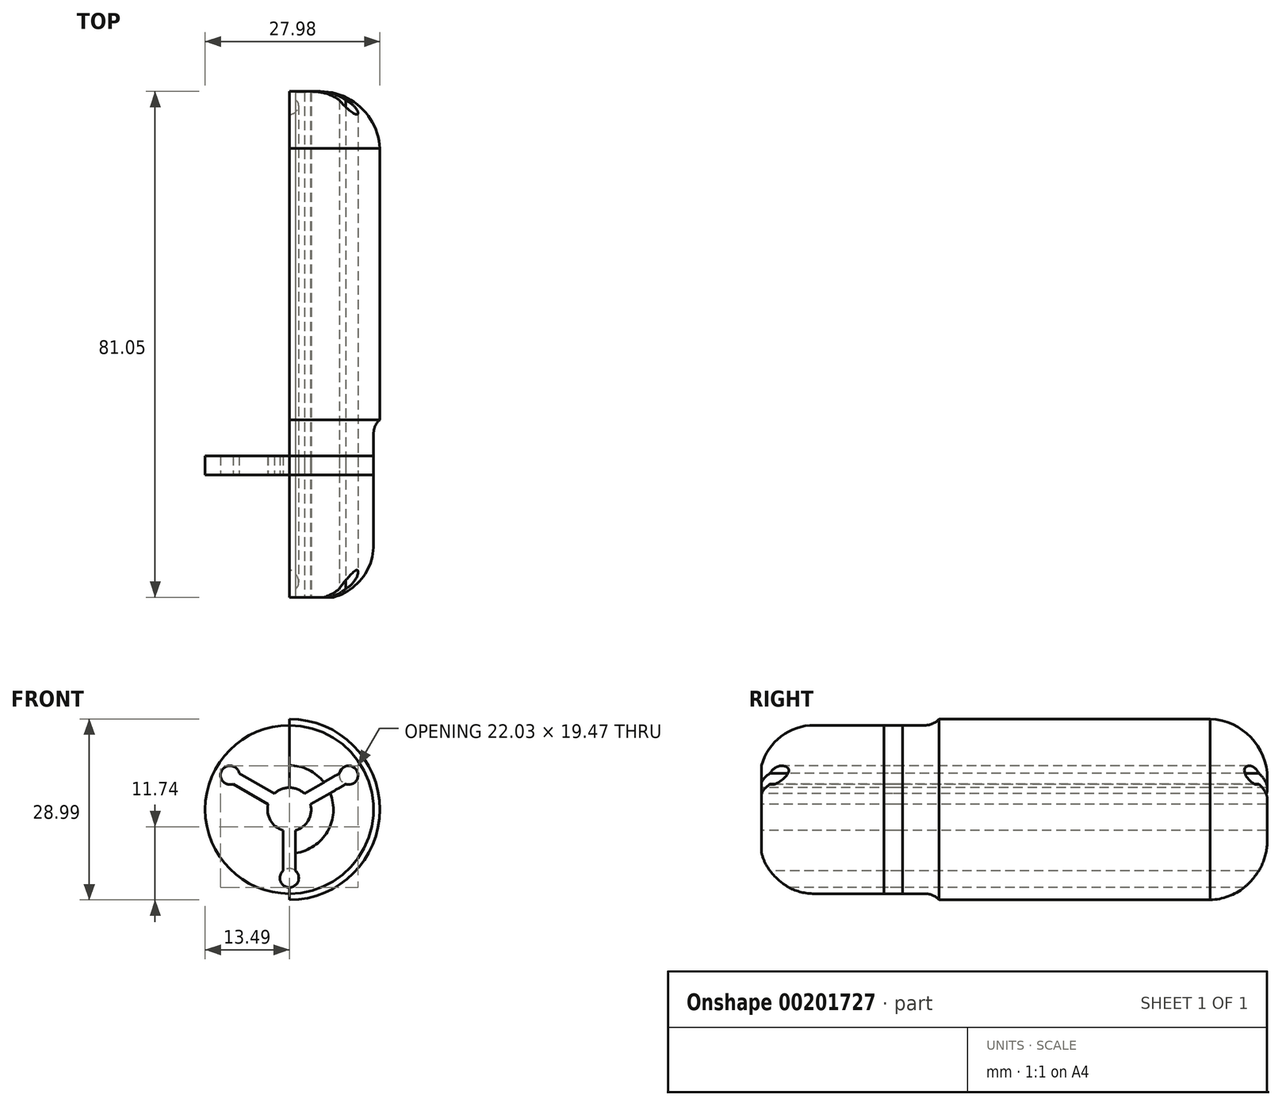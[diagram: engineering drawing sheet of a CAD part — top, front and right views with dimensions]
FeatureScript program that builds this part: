
annotation { "Feature Type Name" : "Feature", "Feature Type Description" : "" }
export const myFeature = defineFeature(function(context is Context, id is Id, definition is map)
    precondition{}
    {
        {
            var Q0;
            Q0=qCreatedBy(makeId("Right.planeOp"),FACE);
            var sketch = newSketch(context, id + "F0", { "sketchPlane" : qUnion([Q0])});
            skLineSegment(sketch, "E0.bottom", {"start": v(-3.13, 33.38) * mm, "end": v(86.87, 33.38) * mm});
            skLineSegment(sketch, "E0.top", {"start": v(-3.13, 32.38) * mm, "end": v(4.08, 32.38) * mm});
            skLineSegment(sketch, "E0.left", {"start": v(-3.13, 33.38) * mm, "end": v(-3.13, 32.38) * mm});
            skLineSegment(sketch, "E0.right", {"start": v(86.87, 33.38) * mm, "end": v(86.87, 32.38) * mm});
            skPoint(sketch, "E0.middle", {"position": v(41.87, 32.88) * mm});
            skLineSegment(sketch, "E1.bottom", {"start": v(86.87, 32.38) * mm, "end": v(81.87, 32.38) * mm, "construction": true});
            skLineSegment(sketch, "E1.top", {"start": v(86.87, 21.38) * mm, "end": v(85.87, 21.38) * mm});
            skLineSegment(sketch, "E1.left", {"start": v(86.87, 32.38) * mm, "end": v(86.87, 21.38) * mm, "construction": true});
            skLineSegment(sketch, "E1.right", {"start": v(81.87, 32.38) * mm, "end": v(81.87, 21.38) * mm, "construction": true});
            skLineSegment(sketch, "E2.bottom", {"start": v(81.87, 32.38) * mm, "end": v(71.87, 32.38) * mm, "construction": true});
            skLineSegment(sketch, "E2.top", {"start": v(81.87, 21.38) * mm, "end": v(71.87, 21.38) * mm, "construction": true});
            skLineSegment(sketch, "E2.right", {"start": v(71.87, 33.38) * mm, "end": v(71.87, 21.38) * mm, "construction": true});
            skLineSegment(sketch, "E3.0", {"start": v(85.87, 22.38) * mm, "end": v(85.37, 22.38) * mm, "construction": true});
            skLineSegment(sketch, "E4.0", {"start": v(85.87, 32.38) * mm, "end": v(85.87, 21.38) * mm, "construction": true});
            skArc(sketch, "E5", {"start": v(82.3, 22.38) * mm, "mid": v(80.84, 28.3) * mm, "end": v(76.33, 32.38) * mm});
            skArc(sketch, "E6", {"start": v(81.87, 21.38) * mm, "mid": v(79.3, 29.1) * mm, "end": v(71.87, 32.38) * mm});
            skLineSegment(sketch, "E7.trimOffspring", {"start": v(76.33, 32.38) * mm, "end": v(86.87, 32.38) * mm});
            skLineSegment(sketch, "E8.top", {"start": v(86.87, 25.38) * mm, "end": v(85.87, 25.38) * mm});
            skLineSegment(sketch, "E8.left", {"start": v(86.87, 23.38) * mm, "end": v(86.87, 25.38) * mm});
            skLineSegment(sketch, "E8.right", {"start": v(85.87, 22.38) * mm, "end": v(85.87, 22.72) * mm, "construction": true});
            skLineSegment(sketch, "E9.bottom", {"start": v(-3.13, 32.38) * mm, "end": v(-2.13, 32.38) * mm, "construction": true});
            skLineSegment(sketch, "E9.top", {"start": v(-3.13, 21.38) * mm, "end": v(-2.13, 21.38) * mm});
            skLineSegment(sketch, "E9.left", {"start": v(-3.13, 32.38) * mm, "end": v(-3.13, 21.38) * mm, "construction": true});
            skLineSegment(sketch, "E9.right", {"start": v(-2.13, 32.38) * mm, "end": v(-2.13, 21.38) * mm, "construction": true});
            skLineSegment(sketch, "E10.bottom", {"start": v(-2.13, 32.38) * mm, "end": v(4.08, 32.38) * mm, "construction": true});
            skLineSegment(sketch, "E10.top", {"start": v(-2.13, 33.38) * mm, "end": v(8.87, 33.38) * mm, "construction": true});
            skLineSegment(sketch, "E10.left", {"start": v(-2.13, 32.38) * mm, "end": v(-2.13, 33.38) * mm, "construction": true});
            skLineSegment(sketch, "E10.right", {"start": v(8.87, 32.38) * mm, "end": v(8.87, 33.38) * mm, "construction": true});
            skArc(sketch, "E11", {"start": v(4.08, 32.38) * mm, "mid": v(-1.17, 27.96) * mm, "end": v(-3.13, 21.38) * mm});
            skArc(sketch, "E12", {"start": v(8.87, 32.38) * mm, "mid": v(1.1, 29.16) * mm, "end": v(-2.13, 21.38) * mm});
            skLineSegment(sketch, "E13.trimOffspring", {"start": v(8.87, 32.38) * mm, "end": v(71.87, 32.38) * mm});
            skLineSegment(sketch, "E14", {"start": v(8.87, 21.38) * mm, "end": v(71.87, 21.38) * mm, "construction": true});
            skLineSegment(sketch, "E15.0", {"start": v(8.87, 17.38) * mm, "end": v(71.87, 17.38) * mm, "construction": true});
            skLineSegment(sketch, "E16.0", {"start": v(86.87, 23.38) * mm, "end": v(85.87, 23.38) * mm, "construction": true});
            skLineSegment(sketch, "E17.0", {"start": v(83.87, 21.38) * mm, "end": v(83.87, 25.38) * mm, "construction": true});
            skLineSegment(sketch, "E18", {"start": v(86.87, 23.38) * mm, "end": v(83.87, 21.38) * mm});
            skLineSegment(sketch, "E19.0", {"start": v(85.87, 23.92) * mm, "end": v(83.57, 22.38) * mm});
            skLineSegment(sketch, "E20.trimOffspring", {"start": v(83.87, 21.38) * mm, "end": v(81.87, 21.38) * mm});
            skLineSegment(sketch, "E21.trimOffspring", {"start": v(83.57, 22.38) * mm, "end": v(82.3, 22.38) * mm});
            skLineSegment(sketch, "E22.trimOffspring", {"start": v(85.87, 23.92) * mm, "end": v(85.87, 25.38) * mm});
            skLineSegment(sketch, "E23.bottom", {"start": v(8.87, 17.38) * mm, "end": v(-3.13, 17.38) * mm, "construction": true});
            skLineSegment(sketch, "E23.top", {"start": v(8.87, 21.38) * mm, "end": v(-3.13, 21.38) * mm, "construction": true});
            skLineSegment(sketch, "E23.left", {"start": v(8.87, 17.38) * mm, "end": v(8.87, 21.38) * mm, "construction": true});
            skLineSegment(sketch, "E23.right", {"start": v(-3.13, 17.38) * mm, "end": v(-3.13, 21.38) * mm, "construction": true});
            skSolve(sketch);
        }
        {
            var Q0;
            Q0=qCreatedBy(makeId("Right.planeOp"),FACE);
            var sketch = newSketch(context, id + "F1", { "sketchPlane" : qUnion([Q0])});
            skLineSegment(sketch, "E24.bottom", {"start": v(-3.13, 33.38) * mm, "end": v(28.58, 33.38) * mm, "construction": true});
            skLineSegment(sketch, "E24.left", {"start": v(-3.13, 33.38) * mm, "end": v(-3.13, 23.38) * mm, "construction": true});
            skLineSegment(sketch, "E24.right", {"start": v(28.58, 33.38) * mm, "end": v(28.58, 33.38) * mm});
            skLineSegment(sketch, "E25", {"start": v(28.58, 32.38) * mm, "end": v(8.84, 32.38) * mm, "construction": true});
            skArc(sketch, "E26", {"start": v(8.84, 32.38) * mm, "mid": v(1.84, 29.83) * mm, "end": v(-1.88, 23.38) * mm, "construction": true});
            skLineSegment(sketch, "E27.0", {"start": v(27.9, 31.88) * mm, "end": v(8.84, 31.88) * mm});
            skArc(sketch, "E28.0", {"start": v(8.84, 31.88) * mm, "mid": v(2.16, 29.45) * mm, "end": v(-1.38, 23.3) * mm});
            skLineSegment(sketch, "E29.0", {"start": v(26.58, 31.38) * mm, "end": v(8.84, 31.38) * mm});
            skArc(sketch, "E30.0", {"start": v(8.84, 30.88) * mm, "mid": v(2.9, 28.77) * mm, "end": v(-0.35, 23.38) * mm, "construction": true});
            skPoint(sketch, "E31.newPointB", {"position": v(28.58, 23.38) * mm});
            skArc(sketch, "E31.filletArc", {"start": v(26.58, 31.38) * mm, "mid": v(27.3, 31.5) * mm, "end": v(27.9, 31.88) * mm});
            skArc(sketch, "E32", {"start": v(8.84, 31.38) * mm, "mid": v(2.64, 29.01) * mm, "end": v(-0.4, 23.12) * mm});
            skLineSegment(sketch, "E33.trimOffspring", {"start": v(-1.37, 23.38) * mm, "end": v(-0.35, 23.38) * mm});
            skSolve(sketch);
        }
        {
            var Q0;
            Q0=qCreatedBy(makeId("Right.planeOp"),FACE);
            var sketch = newSketch(context, id + "F2", { "sketchPlane" : qUnion([Q0])});
            skLineSegment(sketch, "E34", {"start": v(86.87, 23.38) * mm, "end": v(83.87, 21.38) * mm, "construction": true});
            skLineSegment(sketch, "E35", {"start": v(83.87, 21.38) * mm, "end": v(81.87, 21.38) * mm, "construction": true});
            skLineSegment(sketch, "E36.0", {"start": v(86.87, 22.78) * mm, "end": v(84.02, 20.88) * mm});
            skLineSegment(sketch, "E37.0", {"start": v(84.02, 20.88) * mm, "end": v(81.87, 20.88) * mm});
            skLineSegment(sketch, "E38", {"start": v(86.87, 22.78) * mm, "end": v(86.87, 17.38) * mm});
            skLineSegment(sketch, "E39.0", {"start": v(66.87, 20.38) * mm, "end": v(66.87, 17.38) * mm});
            skLineSegment(sketch, "E40.0", {"start": v(81.87, 20.38) * mm, "end": v(66.87, 20.38) * mm});
            skLineSegment(sketch, "E41", {"start": v(71.87, 17.38) * mm, "end": v(66.87, 17.38) * mm});
            skLineSegment(sketch, "E42", {"start": v(71.87, 17.38) * mm, "end": v(86.87, 17.38) * mm});
            skLineSegment(sketch, "E43.0", {"start": v(81.87, 20.88) * mm, "end": v(81.87, 20.38) * mm});
            skSolve(sketch);
        }
        {
            var Q0;
            Q0=qCreatedBy(makeId("Right.planeOp"),FACE);
            var sketch = newSketch(context, id + "F3", { "sketchPlane" : qUnion([Q0])});
            skArc(sketch, "E44", {"start": v(81.87, 21.38) * mm, "mid": v(79.3, 29.1) * mm, "end": v(71.87, 32.38) * mm, "construction": true});
            skArc(sketch, "E45.0", {"start": v(81.3, 20.88) * mm, "mid": v(79.25, 28.4) * mm, "end": v(72.28, 31.88) * mm});
            skLineSegment(sketch, "E46", {"start": v(81.87, 20.38) * mm, "end": v(69.18, 20.38) * mm, "construction": true});
            skLineSegment(sketch, "E47", {"start": v(28.58, 32.38) * mm, "end": v(37.05, 32.38) * mm});
            skLineSegment(sketch, "E48", {"start": v(26.58, 31.38) * mm, "end": v(22.5, 31.38) * mm});
            skArc(sketch, "E49", {"start": v(26.58, 31.38) * mm, "mid": v(27.7, 31.64) * mm, "end": v(28.58, 32.38) * mm});
            skLineSegment(sketch, "E50.0", {"start": v(28.58, 31.88) * mm, "end": v(72.28, 31.88) * mm});
            skArc(sketch, "E51.0", {"start": v(26.58, 30.88) * mm, "mid": v(27.93, 31.2) * mm, "end": v(28.98, 32.08) * mm});
            skLineSegment(sketch, "E52.0", {"start": v(26.58, 30.88) * mm, "end": v(8.74, 30.88) * mm});
            skLineSegment(sketch, "E53.0", {"start": v(81.3, 20.88) * mm, "end": v(0.37, 20.88) * mm});
            skArc(sketch, "E54", {"start": v(8.84, 31.38) * mm, "mid": v(2.74, 29.11) * mm, "end": v(-0.35, 23.38) * mm, "construction": true});
            skArc(sketch, "E55.0", {"start": v(8.83, 30.88) * mm, "mid": v(3.5, 29.1) * mm, "end": v(0.37, 24.44) * mm});
            skLineSegment(sketch, "E56", {"start": v(-2.13, 27.58) * mm, "end": v(-2.13, 15.19) * mm, "construction": true});
            skLineSegment(sketch, "E57.trimOffspring", {"start": v(0.37, 24.44) * mm, "end": v(0.37, 20.88) * mm});
            skSolve(sketch);
        }
        {
            var Q0;
            Q0=qSketchRegion(id+"F3",true);
            var Q1;
            Q1=sQuery(id+"F0.wireOp",EDGE,"E15.0");
            revolve(context, id + "F4", {"entities" : qUnion([Q0]), "axis" : qUnion([Q1]), "revolveType" : RevolveType.ONE_DIRECTION, "angle" : 180 * degree});
        }
        {
            var Q0;
            Q0=qCreatedBy(makeId("Front.planeOp"),FACE);
            var sketch = newSketch(context, id + "F5", { "sketchPlane" : qUnion([Q0])});
            skCircle(sketch, "E58", {"center": v(0, 17.38) * mm, "radius": 14.5 * mm, "construction": true});
            skCircle(sketch, "E59", {"center": v(0, 17.38) * mm, "radius": 3.5 * mm});
            skLineSegment(sketch, "E60", {"start": v(0, 17.38) * mm, "end": v(0, 4.9) * mm, "construction": true});
            skPoint(sketch, "E61", {"position": v(0, 4.9) * mm});
            skPoint(sketch, "E62", {"position": v(-16.26, 26.77) * mm});
            skLineSegment(sketch, "E63.0", {"start": v(-1, 14.03) * mm, "end": v(-1, 7.54) * mm});
            skLineSegment(sketch, "E64.0", {"start": v(1, 14.03) * mm, "end": v(1, 7.54) * mm});
            skArc(sketch, "E65", {"start": v(-1, 7.54) * mm, "mid": v(0, 4.9) * mm, "end": v(1, 7.54) * mm});
            skSolve(sketch);
        }
        {
            var Q0;
            {var subQ0=sQuery(id+"F5.wireOp",EDGE,"E63.0");Q0=makeQuery(id+"F5.imprint","IMPRINT",FACE,{"disambiguationData":[TD([[makeQuery(id+"F5.imprint","IMPRINT",EDGE,{"derivedFrom":subQ0}),1.0]])]});}
            extrude(context, id + "F6", {"entities" : qUnion([Q0]), "oppositeDirection" : true, "depth" : 90 * mm});
        }
        {
            var Q0;
            Q0=qCreatedBy(makeId("Right.planeOp"),FACE);
            var sketch = newSketch(context, id + "F7", { "sketchPlane" : qUnion([Q0])});
            skLineSegment(sketch, "E66", {"start": v(0, 17.38) * mm, "end": v(41.07, 17.38) * mm});
            skSolve(sketch);
        }
        {
            var Q0;
            Q0=makeQuery(id+"F6.opExtrude","SWEPT_BODY",BODY,{"disambiguationData":[OSD([sQuery(id+"F5.wireOp",EDGE,"E59"),sQuery(id+"F5.wireOp",EDGE,"E63.0"),sQuery(id+"F5.wireOp",EDGE,"E64.0"),sQuery(id+"F5.wireOp",EDGE,"E65")])]});
            var Q1;
            Q1=sQuery(id+"F7.wireOp",EDGE,"E66");
            circularPattern(context, id + "F8", {"entities" : qUnion([Q0]), "axis" : qUnion([Q1]), "angle" : 360 * degree, "instanceCount" : 3, "equalSpace" : true});
        }
        {
            var Q0;
            Q0=makeQuery(id+"F6.opExtrude","SWEPT_BODY",BODY,{"disambiguationData":[OSD([sQuery(id+"F5.wireOp",EDGE,"E59"),sQuery(id+"F5.wireOp",EDGE,"E63.0"),sQuery(id+"F5.wireOp",EDGE,"E64.0"),sQuery(id+"F5.wireOp",EDGE,"E65")])]});
            var Q1;
            Q1=makeQuery(id+"F8.opPattern","COPY",BODY,{"derivedFrom":makeQuery(id+"F6.opExtrude","SWEPT_BODY",BODY,{"disambiguationData":[OSD([sQuery(id+"F5.wireOp",EDGE,"E59"),sQuery(id+"F5.wireOp",EDGE,"E63.0"),sQuery(id+"F5.wireOp",EDGE,"E64.0"),sQuery(id+"F5.wireOp",EDGE,"E65")])]}),"instanceName":"2"});
            var Q2;
            Q2=makeQuery(id+"F4.opRevolve","SWEPT_BODY",BODY,{"disambiguationData":[OSD([sQuery(id+"F3.wireOp",EDGE,"E45.0"),sQuery(id+"F3.wireOp",EDGE,"E50.0"),sQuery(id+"F3.wireOp",EDGE,"E51.0"),sQuery(id+"F3.wireOp",EDGE,"E52.0"),sQuery(id+"F3.wireOp",EDGE,"E53.0"),sQuery(id+"F3.wireOp",EDGE,"E55.0"),sQuery(id+"F3.wireOp",EDGE,"E57.trimOffspring")])]});
            booleanBodies(context, id + "F9", {"operationType" : BooleanOperationType.SUBTRACTION, "tools" : qUnion([Q0, Q1]), "targets" : qUnion([Q2]), "keepTools" : true});
        }
        {
            var Q0;
            Q0 = qSketchRegion(id + "F3", true);
            var Q1;
            Q1=sQuery(id+"F0.wireOp",EDGE,"E15.0");
            revolve(context, id + "F10", {"entities" : qUnion([Q0]), "axis" : qUnion([Q1]), "revolveType" : RevolveType.FULL});
        }
        {
            var Q0;
            Q0=qCreatedBy(makeId("Front.planeOp"),FACE);
            var sketch = newSketch(context, id + "F11", { "sketchPlane" : qUnion([Q0])});
            skCircle(sketch, "E67.0", {"center": v(0, 17.38) * mm, "radius": 13.5 * mm});
            skSolve(sketch);
        }
        {
            var Q0;
            Q0 = qSketchRegion(id + "F11", true);
            extrude(context, id + "F12", {"entities" : qUnion([Q0]), "oppositeDirection" : true, "depth" : 23 * mm, "hasSecondDirection" : true, "secondDirectionOppositeDirection" : true, "secondDirectionDepth" : 20 * mm});
        }
        {
            var Q0;
            Q0=makeQuery(id+"F6.opExtrude","SWEPT_BODY",BODY,{"disambiguationData":[OSD([sQuery(id+"F5.wireOp",EDGE,"E59"),sQuery(id+"F5.wireOp",EDGE,"E63.0"),sQuery(id+"F5.wireOp",EDGE,"E64.0"),sQuery(id+"F5.wireOp",EDGE,"E65")])]});
            var Q1;
            Q1=makeQuery(id+"F8.opPattern","COPY",BODY,{"derivedFrom":makeQuery(id+"F6.opExtrude","SWEPT_BODY",BODY,{"disambiguationData":[OSD([sQuery(id+"F5.wireOp",EDGE,"E59"),sQuery(id+"F5.wireOp",EDGE,"E63.0"),sQuery(id+"F5.wireOp",EDGE,"E64.0"),sQuery(id+"F5.wireOp",EDGE,"E65")])]}),"instanceName":"2"});
            var Q2;
            Q2=makeQuery(id+"F8.opPattern","COPY",BODY,{"derivedFrom":makeQuery(id+"F6.opExtrude","SWEPT_BODY",BODY,{"disambiguationData":[OSD([sQuery(id+"F5.wireOp",EDGE,"E59"),sQuery(id+"F5.wireOp",EDGE,"E63.0"),sQuery(id+"F5.wireOp",EDGE,"E64.0"),sQuery(id+"F5.wireOp",EDGE,"E65")])]}),"instanceName":"1"});
            var Q3;
            Q3=makeQuery(id+"F10.opRevolve","SWEPT_BODY",BODY,{"disambiguationData":[OSD([sQuery(id+"F3.wireOp",EDGE,"E45.0"),sQuery(id+"F3.wireOp",EDGE,"E50.0"),sQuery(id+"F3.wireOp",EDGE,"E51.0"),sQuery(id+"F3.wireOp",EDGE,"E52.0"),sQuery(id+"F3.wireOp",EDGE,"E53.0"),sQuery(id+"F3.wireOp",EDGE,"E55.0"),sQuery(id+"F3.wireOp",EDGE,"E57.trimOffspring")])]});
            booleanBodies(context, id + "F13", {"operationType" : BooleanOperationType.SUBTRACTION, "tools" : qUnion([Q0, Q1, Q2]), "targets" : qUnion([Q3])});
        }
        {
            var Q0;
            Q0=makeQuery(id+"F10.opRevolve","SWEPT_BODY",BODY,{"disambiguationData":[OSD([sQuery(id+"F3.wireOp",EDGE,"E45.0"),sQuery(id+"F3.wireOp",EDGE,"E50.0"),sQuery(id+"F3.wireOp",EDGE,"E51.0"),sQuery(id+"F3.wireOp",EDGE,"E52.0"),sQuery(id+"F3.wireOp",EDGE,"E53.0"),sQuery(id+"F3.wireOp",EDGE,"E55.0"),sQuery(id+"F3.wireOp",EDGE,"E57.trimOffspring")])]});
            var Q1;
            Q1=makeQuery(id+"F12.opExtrude","SWEPT_BODY",BODY,{"disambiguationData":[OSD([sQuery(id+"F11.wireOp",EDGE,"E67.0")])]});
            booleanBodies(context, id + "F14", {"operationType" : BooleanOperationType.INTERSECTION, "tools" : qUnion([Q0, Q1])});
        }
    });
